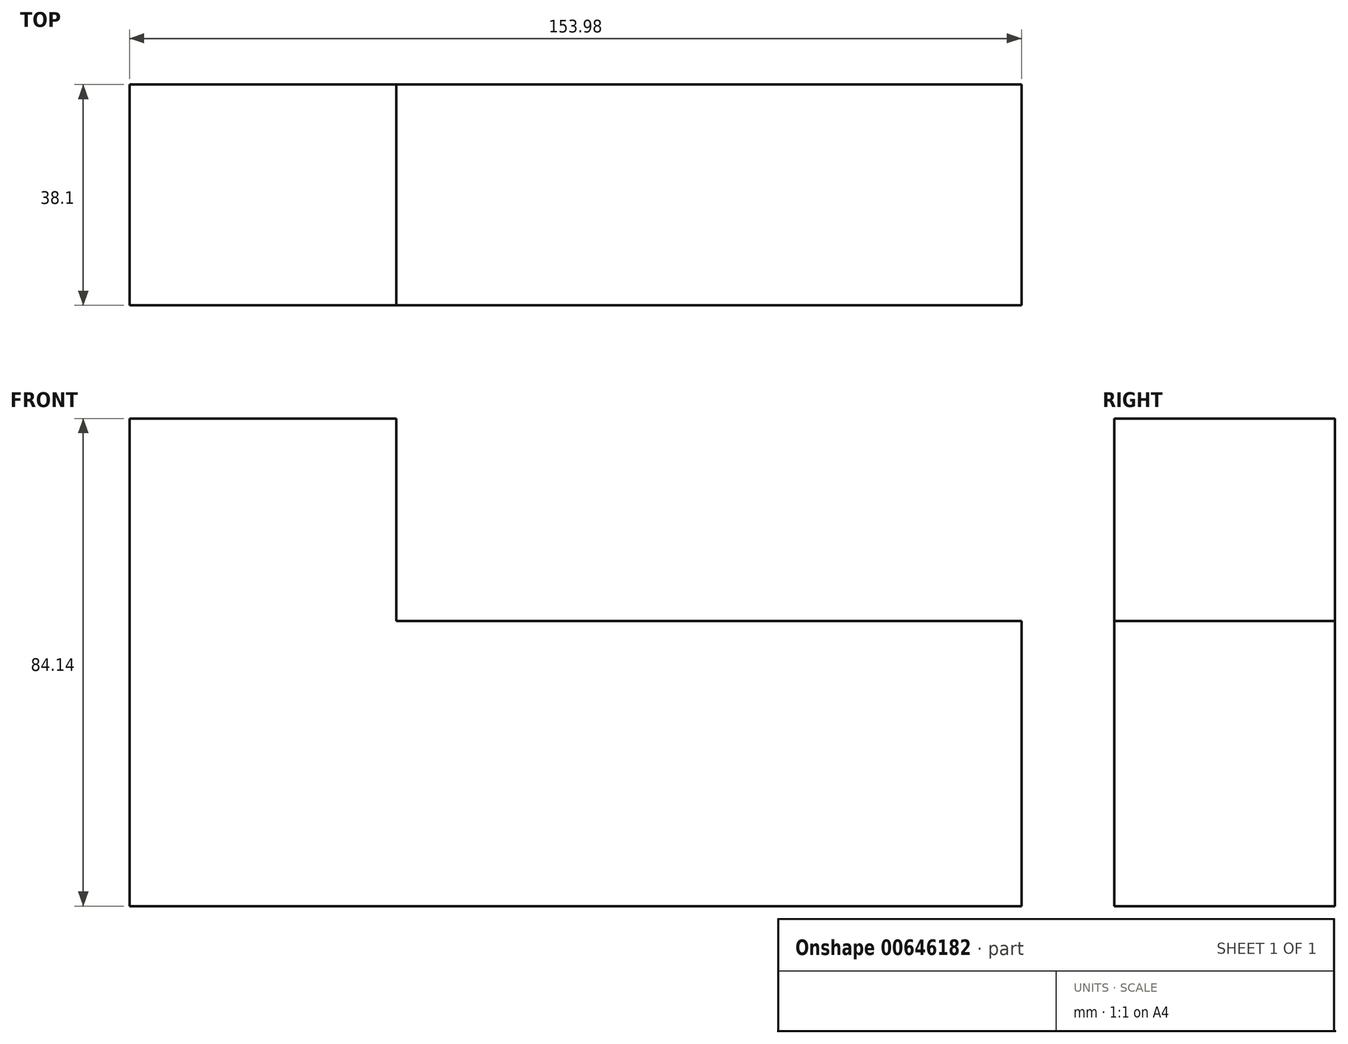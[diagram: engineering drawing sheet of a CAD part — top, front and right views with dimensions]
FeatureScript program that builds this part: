
annotation { "Feature Type Name" : "Feature", "Feature Type Description" : "" }
export const myFeature = defineFeature(function(context is Context, id is Id, definition is map)
    precondition{}
    {
        {
            var Q0;
            Q0=qCreatedBy(makeId("Front.planeOp"),FACE);
            var sketch = newSketch(context, id + "F0", { "sketchPlane" : qUnion([Q0])});
            skLineSegment(sketch, "E0", {"start": v(-40.22, 41.3) * mm, "end": v(-40.22, -42.83) * mm});
            skLineSegment(sketch, "E1", {"start": v(-40.22, -42.83) * mm, "end": v(113.76, -42.83) * mm});
            skLineSegment(sketch, "E2", {"start": v(113.76, -42.83) * mm, "end": v(113.76, 6.38) * mm});
            skLineSegment(sketch, "E3", {"start": v(113.76, 6.38) * mm, "end": v(5.81, 6.38) * mm});
            skLineSegment(sketch, "E4", {"start": v(5.81, 6.38) * mm, "end": v(5.81, 41.3) * mm});
            skLineSegment(sketch, "E5", {"start": v(-40.22, 41.3) * mm, "end": v(5.81, 41.3) * mm});
            skSolve(sketch);
        }
        {
            var Q0;
            Q0=makeQuery(id+"F0.imprint","IMPRINT",FACE,{"disambiguationData":[TD([[makeQuery(id+"F0.imprint","IMPRINT",EDGE,{"derivedFrom":sQuery(id+"F0.wireOp",EDGE,"E0")}),1.0]])]});
            extrude(context, id + "F1", {"entities" : qUnion([Q0]), "depth" : 38.1 * mm, "offsetDistance" : 25.4 * mm});
        }
    });
